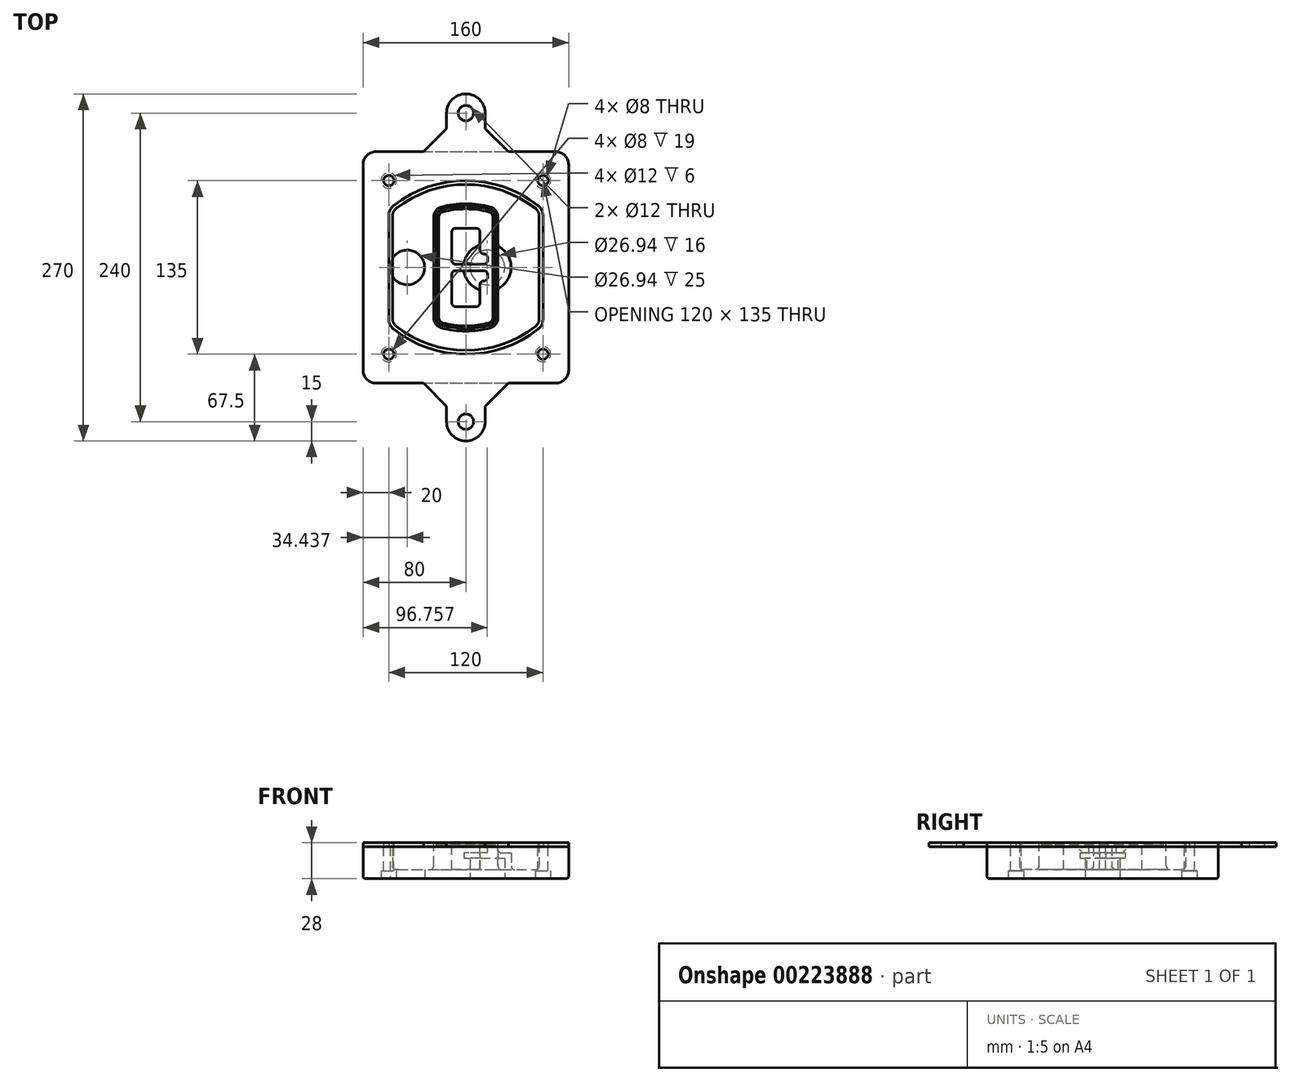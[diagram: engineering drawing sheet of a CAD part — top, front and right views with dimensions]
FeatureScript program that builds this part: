
annotation { "Feature Type Name" : "Feature", "Feature Type Description" : "" }
export const myFeature = defineFeature(function(context is Context, id is Id, definition is map)
    precondition{}
    {
        {
            var Q0;
            Q0=qCreatedBy(makeId("Top.planeOp"),FACE);
            var sketch = newSketch(context, id + "F0", { "sketchPlane" : qUnion([Q0])});
            skPoint(sketch, "E0.rect.middle", {"position": v(0, 0) * mm});
            skLineSegment(sketch, "E1.bottom", {"start": v(-70, -90) * mm, "end": v(70, -90) * mm});
            skLineSegment(sketch, "E1.top", {"start": v(-70, 90) * mm, "end": v(70, 90) * mm});
            skLineSegment(sketch, "E1.left", {"start": v(-80, -80) * mm, "end": v(-80, 80) * mm});
            skLineSegment(sketch, "E1.right", {"start": v(80, -80) * mm, "end": v(80, 80) * mm});
            skLineSegment(sketch, "E2", {"start": v(-80, 90) * mm, "end": v(80, -90) * mm, "construction": true});
            skLineSegment(sketch, "E3", {"start": v(80, 90) * mm, "end": v(-80, -90) * mm, "construction": true});
            skCircle(sketch, "E4", {"center": v(-60, 67.5) * mm, "radius": 4 * mm});
            skCircle(sketch, "E5", {"center": v(60, 67.5) * mm, "radius": 4 * mm});
            skCircle(sketch, "E6", {"center": v(60, -67.5) * mm, "radius": 4 * mm});
            skCircle(sketch, "E7", {"center": v(-60, -67.5) * mm, "radius": 4 * mm});
            skLineSegment(sketch, "E8", {"start": v(-60, 67.5) * mm, "end": v(60, 67.5) * mm, "construction": true});
            skLineSegment(sketch, "E9", {"start": v(60, 67.5) * mm, "end": v(60, -67.5) * mm, "construction": true});
            skLineSegment(sketch, "E10", {"start": v(60, -67.5) * mm, "end": v(-60, -67.5) * mm, "construction": true});
            skLineSegment(sketch, "E11", {"start": v(-60, -67.5) * mm, "end": v(-60, 67.5) * mm, "construction": true});
            skLineSegment(sketch, "E12", {"start": v(-60, 40.3) * mm, "end": v(-60, -40.3) * mm});
            skLineSegment(sketch, "E13", {"start": v(60, 40.3) * mm, "end": v(60, -40.3) * mm});
            skArc(sketch, "E14", {"start": v(56.15, 48.18) * mm, "mid": v(0, 67.5) * mm, "end": v(-56.15, 48.18) * mm});
            skArc(sketch, "E15", {"start": v(-56.15, -48.18) * mm, "mid": v(0, -67.5) * mm, "end": v(56.15, -48.18) * mm});
            skLineSegment(sketch, "E16", {"start": v(-60, 0) * mm, "end": v(60, 0) * mm, "construction": true});
            skPoint(sketch, "E17.visualSharp", {"position": v(-60, -45) * mm});
            skArc(sketch, "E17.filletArc", {"start": v(-60, -40.3) * mm, "mid": v(-58.99, -44.68) * mm, "end": v(-56.15, -48.18) * mm});
            skPoint(sketch, "E18.visualSharp", {"position": v(-60, 45) * mm});
            skArc(sketch, "E18.filletArc", {"start": v(-56.15, 48.18) * mm, "mid": v(-58.99, 44.68) * mm, "end": v(-60, 40.3) * mm});
            skPoint(sketch, "E19.visualSharp", {"position": v(60, 45) * mm});
            skArc(sketch, "E19.filletArc", {"start": v(60, 40.3) * mm, "mid": v(58.99, 44.68) * mm, "end": v(56.15, 48.18) * mm});
            skPoint(sketch, "E20.visualSharp", {"position": v(60, -45) * mm});
            skArc(sketch, "E20.filletArc", {"start": v(56.15, -48.18) * mm, "mid": v(58.99, -44.68) * mm, "end": v(60, -40.3) * mm});
            skPoint(sketch, "E21.visualSharp", {"position": v(-80, 90) * mm});
            skArc(sketch, "E21.filletArc", {"start": v(-70, 90) * mm, "mid": v(-77.07, 87.07) * mm, "end": v(-80, 80) * mm});
            skPoint(sketch, "E22.visualSharp", {"position": v(80, 90) * mm});
            skArc(sketch, "E22.filletArc", {"start": v(80, 80) * mm, "mid": v(77.07, 87.07) * mm, "end": v(70, 90) * mm});
            skPoint(sketch, "E23.visualSharp", {"position": v(80, -90) * mm});
            skArc(sketch, "E23.filletArc", {"start": v(70, -90) * mm, "mid": v(77.07, -87.07) * mm, "end": v(80, -80) * mm});
            skPoint(sketch, "E24.visualSharp", {"position": v(-80, -90) * mm});
            skArc(sketch, "E24.filletArc", {"start": v(-80, -80) * mm, "mid": v(-77.07, -87.07) * mm, "end": v(-70, -90) * mm});
            skArc(sketch, "E25.0", {"start": v(57, 40.3) * mm, "mid": v(56.3, 43.36) * mm, "end": v(54.3, 45.81) * mm});
            skLineSegment(sketch, "E25.1", {"start": v(57, 40.3) * mm, "end": v(57, -40.3) * mm});
            skArc(sketch, "E25.2", {"start": v(54.3, -45.81) * mm, "mid": v(56.3, -43.36) * mm, "end": v(57, -40.3) * mm});
            skArc(sketch, "E25.3", {"start": v(-54.3, -45.81) * mm, "mid": v(0, -64.5) * mm, "end": v(54.3, -45.81) * mm});
            skArc(sketch, "E25.4", {"start": v(-57, -40.3) * mm, "mid": v(-56.3, -43.36) * mm, "end": v(-54.3, -45.81) * mm});
            skArc(sketch, "E25.5", {"start": v(54.3, 45.81) * mm, "mid": v(0, 64.5) * mm, "end": v(-54.3, 45.81) * mm});
            skLineSegment(sketch, "E25.6", {"start": v(-57, 40.3) * mm, "end": v(-57, -40.3) * mm});
            skArc(sketch, "E25.7", {"start": v(-54.3, 45.81) * mm, "mid": v(-56.3, 43.36) * mm, "end": v(-57, 40.3) * mm});
            skArc(sketch, "E26.0", {"start": v(-58.62, 51.33) * mm, "mid": v(-62.58, 46.43) * mm, "end": v(-64, 40.3) * mm});
            skArc(sketch, "E26.1", {"start": v(58.62, 51.33) * mm, "mid": v(0, 71.5) * mm, "end": v(-58.62, 51.33) * mm});
            skArc(sketch, "E26.2", {"start": v(64, 40.3) * mm, "mid": v(62.58, 46.43) * mm, "end": v(58.62, 51.33) * mm});
            skLineSegment(sketch, "E26.3", {"start": v(64, 40.3) * mm, "end": v(64, -40.3) * mm});
            skArc(sketch, "E26.4", {"start": v(58.62, -51.33) * mm, "mid": v(62.58, -46.43) * mm, "end": v(64, -40.3) * mm});
            skLineSegment(sketch, "E26.5", {"start": v(-64, 40.3) * mm, "end": v(-64, -40.3) * mm});
            skArc(sketch, "E26.6", {"start": v(-58.62, -51.33) * mm, "mid": v(0, -71.5) * mm, "end": v(58.62, -51.33) * mm});
            skArc(sketch, "E26.7", {"start": v(-64, -40.3) * mm, "mid": v(-62.58, -46.43) * mm, "end": v(-58.62, -51.33) * mm});
            skSolve(sketch);
        }
        {
            var Q0;
            Q0=makeQuery(id+"F0.imprint","IMPRINT",FACE,{"disambiguationData":[TD([[makeQuery(id+"F0.imprint","IMPRINT",EDGE,{"derivedFrom":sQuery(id+"F0.wireOp",EDGE,"E1.bottom")}),1.0]])]});
            var Q1;
            Q1=makeQuery(id+"F0.imprint","IMPRINT",FACE,{"disambiguationData":[TD([[makeQuery(id+"F0.imprint","IMPRINT",EDGE,{"derivedFrom":sQuery(id+"F0.wireOp",EDGE,"E12")}),1.0]])]});
            var Q2;
            Q2=makeQuery(id+"F0.imprint","IMPRINT",FACE,{"disambiguationData":[TD([[makeQuery(id+"F0.imprint","IMPRINT",EDGE,{"derivedFrom":sQuery(id+"F0.wireOp",EDGE,"E25.0")}),1.0]])]});
            var Q3;
            Q3=makeQuery(id+"F0.imprint","IMPRINT",FACE,{"disambiguationData":[TD([[makeQuery(id+"F0.imprint","IMPRINT",EDGE,{"derivedFrom":sQuery(id+"F0.wireOp",EDGE,"E12")}),-1.0]])]});
            extrude(context, id + "F1", {"entities" : qUnion([Q0, Q1, Q2, Q3]), "oppositeDirection" : true, "depth" : 25 * mm});
        }
        {
            var Q0;
            Q0=makeQuery(id+"F0.imprint","IMPRINT",FACE,{"disambiguationData":[TD([[makeQuery(id+"F0.imprint","IMPRINT",EDGE,{"derivedFrom":sQuery(id+"F0.wireOp",EDGE,"E12")}),1.0]])]});
            extrude(context, id + "F2", {"entities" : qUnion([Q0]), "operationType" : NewBodyOperationType.ADD, "depth" : 3 * mm});
        }
        {
            var Q0;
            Q0=makeQuery(id+"F0.imprint","IMPRINT",FACE,{"disambiguationData":[TD([[makeQuery(id+"F0.imprint","IMPRINT",EDGE,{"derivedFrom":sQuery(id+"F0.wireOp",EDGE,"E25.0")}),1.0]])]});
            extrude(context, id + "F3", {"entities" : qUnion([Q0]), "operationType" : NewBodyOperationType.REMOVE, "oppositeDirection" : true, "depth" : 18 * mm});
        }
        {
            var Q0;
            Q0=makeQuery(id+"F2.opExtrude","CAP_FACE",FACE,{"disambiguationData":[OSD([sQuery(id+"F0.wireOp",EDGE,"E12"),sQuery(id+"F0.wireOp",EDGE,"E13"),sQuery(id+"F0.wireOp",EDGE,"E14"),sQuery(id+"F0.wireOp",EDGE,"E15"),sQuery(id+"F0.wireOp",EDGE,"E17.filletArc"),sQuery(id+"F0.wireOp",EDGE,"E18.filletArc"),sQuery(id+"F0.wireOp",EDGE,"E19.filletArc"),sQuery(id+"F0.wireOp",EDGE,"E20.filletArc"),sQuery(id+"F0.wireOp",EDGE,"E25.0"),sQuery(id+"F0.wireOp",EDGE,"E25.1"),sQuery(id+"F0.wireOp",EDGE,"E25.2"),sQuery(id+"F0.wireOp",EDGE,"E25.3"),sQuery(id+"F0.wireOp",EDGE,"E25.4"),sQuery(id+"F0.wireOp",EDGE,"E25.5"),sQuery(id+"F0.wireOp",EDGE,"E25.6"),sQuery(id+"F0.wireOp",EDGE,"E25.7")])],"isStart":false});
            var sketch = newSketch(context, id + "F4", { "sketchPlane" : qUnion([Q0])});
            skArc(sketch, "E27.0", {"start": v(-19.08, -46.97) * mm, "mid": v(0, -49.5) * mm, "end": v(19.08, -46.97) * mm});
            skArc(sketch, "E28.0", {"start": v(19.08, 46.97) * mm, "mid": v(0, 49.5) * mm, "end": v(-19.08, 46.97) * mm});
            skLineSegment(sketch, "E29", {"start": v(-25, 39.25) * mm, "end": v(-25, -39.25) * mm});
            skLineSegment(sketch, "E30", {"start": v(25, 39.25) * mm, "end": v(25, -39.25) * mm});
            skLineSegment(sketch, "E31", {"start": v(-25, 45.1) * mm, "end": v(25, 45.1) * mm, "construction": true});
            skLineSegment(sketch, "E32", {"start": v(-25, -45.1) * mm, "end": v(25, -45.1) * mm, "construction": true});
            skPoint(sketch, "E33.visualSharp", {"position": v(-25, 45.1) * mm});
            skArc(sketch, "E33.filletArc", {"start": v(-19.08, 46.97) * mm, "mid": v(-23.35, 44.11) * mm, "end": v(-25, 39.25) * mm});
            skPoint(sketch, "E34.visualSharp", {"position": v(25, 45.1) * mm});
            skArc(sketch, "E34.filletArc", {"start": v(25, 39.25) * mm, "mid": v(23.35, 44.11) * mm, "end": v(19.08, 46.97) * mm});
            skPoint(sketch, "E35.visualSharp", {"position": v(25, -45.1) * mm});
            skArc(sketch, "E35.filletArc", {"start": v(19.08, -46.97) * mm, "mid": v(23.35, -44.11) * mm, "end": v(25, -39.25) * mm});
            skPoint(sketch, "E36.visualSharp", {"position": v(-25, -45.1) * mm});
            skArc(sketch, "E36.filletArc", {"start": v(-25, -39.25) * mm, "mid": v(-23.35, -44.11) * mm, "end": v(-19.08, -46.97) * mm});
            skArc(sketch, "E37.0", {"start": v(54.3, 45.81) * mm, "mid": v(0, 64.5) * mm, "end": v(-54.3, 45.81) * mm});
            skArc(sketch, "E37.1", {"start": v(-54.3, 45.81) * mm, "mid": v(-56.3, 43.36) * mm, "end": v(-57, 40.3) * mm});
            skLineSegment(sketch, "E37.2", {"start": v(-57, 40.3) * mm, "end": v(-57, -40.3) * mm});
            skArc(sketch, "E37.3", {"start": v(-57, -40.3) * mm, "mid": v(-56.3, -43.36) * mm, "end": v(-54.3, -45.81) * mm});
            skArc(sketch, "E37.4", {"start": v(-54.3, -45.81) * mm, "mid": v(0, -64.5) * mm, "end": v(54.3, -45.81) * mm});
            skArc(sketch, "E37.5", {"start": v(54.3, -45.81) * mm, "mid": v(56.3, -43.36) * mm, "end": v(57, -40.3) * mm});
            skLineSegment(sketch, "E37.6", {"start": v(57, 40.3) * mm, "end": v(57, -40.3) * mm});
            skArc(sketch, "E37.7", {"start": v(57, 40.3) * mm, "mid": v(56.3, 43.36) * mm, "end": v(54.3, 45.81) * mm});
            skLineSegment(sketch, "E38.0", {"start": v(23, 39.25) * mm, "end": v(23, -39.25) * mm});
            skArc(sketch, "E38.1", {"start": v(18.56, -45.04) * mm, "mid": v(21.76, -42.9) * mm, "end": v(23, -39.25) * mm});
            skArc(sketch, "E38.2", {"start": v(-18.56, -45.04) * mm, "mid": v(0, -47.5) * mm, "end": v(18.56, -45.04) * mm});
            skArc(sketch, "E38.3", {"start": v(-23, -39.25) * mm, "mid": v(-21.76, -42.9) * mm, "end": v(-18.56, -45.04) * mm});
            skLineSegment(sketch, "E38.4", {"start": v(-23, 39.25) * mm, "end": v(-23, -39.25) * mm});
            skArc(sketch, "E38.5", {"start": v(23, 39.25) * mm, "mid": v(21.76, 42.9) * mm, "end": v(18.56, 45.04) * mm});
            skArc(sketch, "E38.6", {"start": v(-18.56, 45.04) * mm, "mid": v(-21.76, 42.9) * mm, "end": v(-23, 39.25) * mm});
            skArc(sketch, "E38.7", {"start": v(18.56, 45.04) * mm, "mid": v(0, 47.5) * mm, "end": v(-18.56, 45.04) * mm});
            skArc(sketch, "E39.0", {"start": v(21, 39.25) * mm, "mid": v(20.18, 41.68) * mm, "end": v(18.04, 43.1) * mm});
            skLineSegment(sketch, "E39.1", {"start": v(21, 39.25) * mm, "end": v(21, -39.25) * mm});
            skArc(sketch, "E39.2", {"start": v(18.04, -43.1) * mm, "mid": v(20.18, -41.68) * mm, "end": v(21, -39.25) * mm});
            skArc(sketch, "E39.3", {"start": v(-18.04, -43.1) * mm, "mid": v(0, -45.5) * mm, "end": v(18.04, -43.1) * mm});
            skArc(sketch, "E39.4", {"start": v(-21, -39.25) * mm, "mid": v(-20.18, -41.68) * mm, "end": v(-18.04, -43.1) * mm});
            skArc(sketch, "E39.5", {"start": v(18.04, 43.1) * mm, "mid": v(0, 45.5) * mm, "end": v(-18.04, 43.1) * mm});
            skLineSegment(sketch, "E39.6", {"start": v(-21, 39.25) * mm, "end": v(-21, -39.25) * mm});
            skArc(sketch, "E39.7", {"start": v(-18.04, 43.1) * mm, "mid": v(-20.18, 41.68) * mm, "end": v(-21, 39.25) * mm});
            skLineSegment(sketch, "E40", {"start": v(-25, 0) * mm, "end": v(25, 0) * mm, "construction": true});
            skLineSegment(sketch, "E41", {"start": v(-11, 5.5) * mm, "end": v(-11, 27.5) * mm});
            skLineSegment(sketch, "E42", {"start": v(-8, 30.5) * mm, "end": v(8, 30.5) * mm});
            skLineSegment(sketch, "E43", {"start": v(11, 27.5) * mm, "end": v(11, 13.5) * mm});
            skLineSegment(sketch, "E44", {"start": v(14, 10.5) * mm, "end": v(14, 10.5) * mm});
            skLineSegment(sketch, "E45", {"start": v(17, 7.5) * mm, "end": v(17, 5.5) * mm});
            skLineSegment(sketch, "E46", {"start": v(14, 2.5) * mm, "end": v(-8, 2.5) * mm});
            skPoint(sketch, "E47.visualSharp", {"position": v(-11, 30.5) * mm});
            skArc(sketch, "E47.filletArc", {"start": v(-8, 30.5) * mm, "mid": v(-10.12, 29.62) * mm, "end": v(-11, 27.5) * mm});
            skPoint(sketch, "E48.visualSharp", {"position": v(11, 30.5) * mm});
            skArc(sketch, "E48.filletArc", {"start": v(11, 27.5) * mm, "mid": v(10.12, 29.62) * mm, "end": v(8, 30.5) * mm});
            skPoint(sketch, "E49.visualSharp", {"position": v(11, 10.5) * mm});
            skArc(sketch, "E49.filletArc", {"start": v(11, 13.5) * mm, "mid": v(11.88, 11.38) * mm, "end": v(14, 10.5) * mm});
            skPoint(sketch, "E50.visualSharp", {"position": v(17, 10.5) * mm});
            skArc(sketch, "E50.filletArc", {"start": v(17, 7.5) * mm, "mid": v(16.12, 9.62) * mm, "end": v(14, 10.5) * mm});
            skPoint(sketch, "E51.visualSharp", {"position": v(17, 2.5) * mm});
            skArc(sketch, "E51.filletArc", {"start": v(14, 2.5) * mm, "mid": v(16.12, 3.38) * mm, "end": v(17, 5.5) * mm});
            skPoint(sketch, "E52.visualSharp", {"position": v(-11, 2.5) * mm});
            skArc(sketch, "E52.filletArc", {"start": v(-11, 5.5) * mm, "mid": v(-10.12, 3.38) * mm, "end": v(-8, 2.5) * mm});
            skLineSegment(sketch, "E53.0.MirrorCS", {"start": v(14, -2.5) * mm, "end": v(-8, -2.5) * mm});
            skArc(sketch, "E54.0.MirrorCS", {"start": v(-11, -5.5) * mm, "mid": v(-10.12, -3.38) * mm, "end": v(-8, -2.5) * mm});
            skLineSegment(sketch, "E55.0.MirrorCS", {"start": v(-11, -5.5) * mm, "end": v(-11, -27.5) * mm});
            skArc(sketch, "E56.0.MirrorCS", {"start": v(-8, -30.5) * mm, "mid": v(-10.12, -29.62) * mm, "end": v(-11, -27.5) * mm});
            skLineSegment(sketch, "E57.0.MirrorCS", {"start": v(-8, -30.5) * mm, "end": v(8, -30.5) * mm});
            skArc(sketch, "E58.0.MirrorCS", {"start": v(11, -27.5) * mm, "mid": v(10.12, -29.62) * mm, "end": v(8, -30.5) * mm});
            skLineSegment(sketch, "E59.0.MirrorCS", {"start": v(11, -27.5) * mm, "end": v(11, -13.5) * mm});
            skArc(sketch, "E60.0.MirrorCS", {"start": v(11, -13.5) * mm, "mid": v(11.88, -11.38) * mm, "end": v(14, -10.5) * mm});
            skArc(sketch, "E61.0.MirrorCS", {"start": v(17, -7.5) * mm, "mid": v(16.12, -9.62) * mm, "end": v(14, -10.5) * mm});
            skLineSegment(sketch, "E62.0.MirrorCS", {"start": v(17, -7.5) * mm, "end": v(17, -5.5) * mm});
            skArc(sketch, "E63.0.MirrorCS", {"start": v(14, -2.5) * mm, "mid": v(16.12, -3.38) * mm, "end": v(17, -5.5) * mm});
            skSolve(sketch);
        }
        {
            var Q0;
            Q0=makeQuery(id+"F4.imprint","IMPRINT",FACE,{"disambiguationData":[TD([[makeQuery(id+"F4.imprint","IMPRINT",EDGE,{"derivedFrom":sQuery(id+"F4.wireOp",EDGE,"E27.0")}),1.0]])]});
            var Q1;
            Q1=makeQuery(id+"F4.imprint","IMPRINT",FACE,{"disambiguationData":[TD([[makeQuery(id+"F4.imprint","IMPRINT",EDGE,{"derivedFrom":sQuery(id+"F4.wireOp",EDGE,"E38.0")}),-1.0]])]});
            var Q2;
            Q2=makeQuery(id+"F4.imprint","IMPRINT",FACE,{"disambiguationData":[TD([[makeQuery(id+"F4.imprint","IMPRINT",EDGE,{"derivedFrom":sQuery(id+"F4.wireOp",EDGE,"E39.0")}),1.0]])]});
            extrude(context, id + "F5", {"entities" : qUnion([Q0, Q1, Q2]), "operationType" : NewBodyOperationType.ADD, "endBound" : BoundingType.UP_TO_NEXT, "oppositeDirection" : true, "depth" : 25 * mm});
        }
        {
            var Q0;
            Q0=makeQuery(id+"F4.imprint","IMPRINT",FACE,{"disambiguationData":[TD([[makeQuery(id+"F4.imprint","IMPRINT",EDGE,{"derivedFrom":sQuery(id+"F4.wireOp",EDGE,"E38.0")}),-1.0]])]});
            extrude(context, id + "F6", {"entities" : qUnion([Q0]), "operationType" : NewBodyOperationType.REMOVE, "oppositeDirection" : true, "depth" : 2 * mm});
        }
        {
            var Q0;
            Q0=makeQuery(id+"F1.opExtrude","CAP_FACE",FACE,{"disambiguationData":[OSD([sQuery(id+"F0.wireOp",EDGE,"E1.bottom"),sQuery(id+"F0.wireOp",EDGE,"E1.top"),sQuery(id+"F0.wireOp",EDGE,"E1.left"),sQuery(id+"F0.wireOp",EDGE,"E1.right"),sQuery(id+"F0.wireOp",EDGE,"E4"),sQuery(id+"F0.wireOp",EDGE,"E5"),sQuery(id+"F0.wireOp",EDGE,"E6"),sQuery(id+"F0.wireOp",EDGE,"E7"),sQuery(id+"F0.wireOp",EDGE,"E21.filletArc"),sQuery(id+"F0.wireOp",EDGE,"E22.filletArc"),sQuery(id+"F0.wireOp",EDGE,"E23.filletArc"),sQuery(id+"F0.wireOp",EDGE,"E24.filletArc")])],"isStart":false});
            var sketch = newSketch(context, id + "F7", { "sketchPlane" : qUnion([Q0])});
            skCircle(sketch, "E64", {"center": v(16.76, 0) * mm, "radius": 13.47 * mm});
            skCircle(sketch, "E65", {"center": v(-45.56, 0) * mm, "radius": 13.47 * mm});
            skLineSegment(sketch, "E66", {"start": v(80, 0) * mm, "end": v(-80, 0) * mm});
            skCircle(sketch, "E67", {"center": v(16.76, 0) * mm, "radius": 18.47 * mm});
            skCircle(sketch, "E68", {"center": v(60, -67.5) * mm, "radius": 6 * mm});
            skCircle(sketch, "E69", {"center": v(-60, -67.5) * mm, "radius": 6 * mm});
            skCircle(sketch, "E70", {"center": v(-60, 67.5) * mm, "radius": 6 * mm});
            skCircle(sketch, "E71", {"center": v(60, 67.5) * mm, "radius": 6 * mm});
            skSolve(sketch);
        }
        {
            var Q0;
            {var subQ1=sQuery(id+"F7.wireOp",EDGE,"E66");var subQ4=sQuery(id+"F7.wireOp",EDGE,"E64");var subQ6=makeQuery(id+"F7.imprint","INTERSECT",VERTEX,{"disambiguationData":[OD(0.0)],"derivedFrom":[subQ4,subQ1]});Q0=makeQuery(id+"F7.imprint","IMPRINT",FACE,{"disambiguationData":[TD([[makeQuery(id+"F7.imprint","IMPRINT",EDGE,{"disambiguationData":[TD([[subQ6,-1.0]])],"derivedFrom":subQ4}),-1.0]])]});}
            var Q1;
            {var subQ0=sQuery(id+"F7.wireOp",EDGE,"E66");var subQ1=sQuery(id+"F7.wireOp",EDGE,"E64");var subQ3=makeQuery(id+"F7.imprint","INTERSECT",VERTEX,{"disambiguationData":[OD(0.0)],"derivedFrom":[subQ1,subQ0]});Q1=makeQuery(id+"F7.imprint","IMPRINT",FACE,{"disambiguationData":[TD([[makeQuery(id+"F7.imprint","IMPRINT",EDGE,{"disambiguationData":[TD([[subQ3,-1.0]])],"derivedFrom":subQ1}),1.0]])]});}
            var Q2;
            {var subQ0=sQuery(id+"F7.wireOp",EDGE,"E66");var subQ1=sQuery(id+"F7.wireOp",EDGE,"E64");var subQ3=makeQuery(id+"F7.imprint","INTERSECT",VERTEX,{"disambiguationData":[OD(0.0)],"derivedFrom":[subQ1,subQ0]});Q2=makeQuery(id+"F7.imprint","IMPRINT",FACE,{"disambiguationData":[TD([[makeQuery(id+"F7.imprint","IMPRINT",EDGE,{"disambiguationData":[TD([[subQ3,1.0]])],"derivedFrom":subQ1}),1.0]])]});}
            var Q3;
            {var subQ1=sQuery(id+"F7.wireOp",EDGE,"E66");var subQ4=sQuery(id+"F7.wireOp",EDGE,"E64");var subQ6=makeQuery(id+"F7.imprint","INTERSECT",VERTEX,{"disambiguationData":[OD(0.0)],"derivedFrom":[subQ4,subQ1]});Q3=makeQuery(id+"F7.imprint","IMPRINT",FACE,{"disambiguationData":[TD([[makeQuery(id+"F7.imprint","IMPRINT",EDGE,{"disambiguationData":[TD([[subQ6,1.0]])],"derivedFrom":subQ4}),-1.0]])]});}
            extrude(context, id + "F8", {"entities" : qUnion([Q0, Q1, Q2, Q3]), "operationType" : NewBodyOperationType.ADD, "oppositeDirection" : true, "depth" : 20 * mm});
        }
        {
            var Q0;
            {var subQ0=sQuery(id+"F7.wireOp",EDGE,"E66");var subQ1=sQuery(id+"F7.wireOp",EDGE,"E64");var subQ3=makeQuery(id+"F7.imprint","INTERSECT",VERTEX,{"disambiguationData":[OD(0.0)],"derivedFrom":[subQ1,subQ0]});Q0=makeQuery(id+"F7.imprint","IMPRINT",FACE,{"disambiguationData":[TD([[makeQuery(id+"F7.imprint","IMPRINT",EDGE,{"disambiguationData":[TD([[subQ3,-1.0]])],"derivedFrom":subQ1}),1.0]])]});}
            var Q1;
            {var subQ0=sQuery(id+"F7.wireOp",EDGE,"E66");var subQ1=sQuery(id+"F7.wireOp",EDGE,"E64");var subQ3=makeQuery(id+"F7.imprint","INTERSECT",VERTEX,{"disambiguationData":[OD(0.0)],"derivedFrom":[subQ1,subQ0]});Q1=makeQuery(id+"F7.imprint","IMPRINT",FACE,{"disambiguationData":[TD([[makeQuery(id+"F7.imprint","IMPRINT",EDGE,{"disambiguationData":[TD([[subQ3,1.0]])],"derivedFrom":subQ1}),1.0]])]});}
            extrude(context, id + "F9", {"entities" : qUnion([Q0, Q1]), "operationType" : NewBodyOperationType.REMOVE, "oppositeDirection" : true, "depth" : 16 * mm});
        }
        {
            var Q0;
            {var subQ0=sQuery(id+"F7.wireOp",EDGE,"E66");var subQ1=sQuery(id+"F7.wireOp",EDGE,"E65");var subQ3=makeQuery(id+"F7.imprint","INTERSECT",VERTEX,{"disambiguationData":[OD(0.0)],"derivedFrom":[subQ1,subQ0]});Q0=makeQuery(id+"F7.imprint","IMPRINT",FACE,{"disambiguationData":[TD([[makeQuery(id+"F7.imprint","IMPRINT",EDGE,{"disambiguationData":[TD([[subQ3,-1.0]])],"derivedFrom":subQ1}),1.0]])]});}
            var Q1;
            {var subQ0=sQuery(id+"F7.wireOp",EDGE,"E66");var subQ1=sQuery(id+"F7.wireOp",EDGE,"E65");var subQ3=makeQuery(id+"F7.imprint","INTERSECT",VERTEX,{"disambiguationData":[OD(0.0)],"derivedFrom":[subQ1,subQ0]});Q1=makeQuery(id+"F7.imprint","IMPRINT",FACE,{"disambiguationData":[TD([[makeQuery(id+"F7.imprint","IMPRINT",EDGE,{"disambiguationData":[TD([[subQ3,1.0]])],"derivedFrom":subQ1}),1.0]])]});}
            extrude(context, id + "F10", {"entities" : qUnion([Q0, Q1]), "operationType" : NewBodyOperationType.REMOVE, "oppositeDirection" : true, "depth" : 25 * mm});
        }
        {
            var Q0;
            Q0=makeQuery(id+"F7.imprint","IMPRINT",FACE,{"disambiguationData":[TD([[makeQuery(id+"F7.imprint","IMPRINT",EDGE,{"derivedFrom":sQuery(id+"F7.wireOp",EDGE,"E68")}),1.0]])]});
            var Q1;
            Q1=makeQuery(id+"F7.imprint","IMPRINT",FACE,{"disambiguationData":[TD([[makeQuery(id+"F7.imprint","IMPRINT",EDGE,{"derivedFrom":makeQuery(id+"F1.opExtrude","CAP_EDGE",EDGE,{"disambiguationData":[OSD([sQuery(id+"F0.wireOp",EDGE,"E5")])],"isStart":false})}),-1.0]])]});
            var Q2;
            Q2=makeQuery(id+"F7.imprint","IMPRINT",FACE,{"disambiguationData":[TD([[makeQuery(id+"F7.imprint","IMPRINT",EDGE,{"derivedFrom":sQuery(id+"F7.wireOp",EDGE,"E69")}),1.0]])]});
            var Q3;
            Q3=makeQuery(id+"F7.imprint","IMPRINT",FACE,{"disambiguationData":[TD([[makeQuery(id+"F7.imprint","IMPRINT",EDGE,{"derivedFrom":makeQuery(id+"F1.opExtrude","CAP_EDGE",EDGE,{"disambiguationData":[OSD([sQuery(id+"F0.wireOp",EDGE,"E4")])],"isStart":false})}),-1.0]])]});
            var Q4;
            Q4=makeQuery(id+"F7.imprint","IMPRINT",FACE,{"disambiguationData":[TD([[makeQuery(id+"F7.imprint","IMPRINT",EDGE,{"derivedFrom":sQuery(id+"F7.wireOp",EDGE,"E70")}),1.0]])]});
            var Q5;
            Q5=makeQuery(id+"F7.imprint","IMPRINT",FACE,{"disambiguationData":[TD([[makeQuery(id+"F7.imprint","IMPRINT",EDGE,{"derivedFrom":makeQuery(id+"F1.opExtrude","CAP_EDGE",EDGE,{"disambiguationData":[OSD([sQuery(id+"F0.wireOp",EDGE,"E7")])],"isStart":false})}),-1.0]])]});
            var Q6;
            Q6=makeQuery(id+"F7.imprint","IMPRINT",FACE,{"disambiguationData":[TD([[makeQuery(id+"F7.imprint","IMPRINT",EDGE,{"derivedFrom":sQuery(id+"F7.wireOp",EDGE,"E71")}),1.0]])]});
            var Q7;
            Q7=makeQuery(id+"F7.imprint","IMPRINT",FACE,{"disambiguationData":[TD([[makeQuery(id+"F7.imprint","IMPRINT",EDGE,{"derivedFrom":makeQuery(id+"F1.opExtrude","CAP_EDGE",EDGE,{"disambiguationData":[OSD([sQuery(id+"F0.wireOp",EDGE,"E6")])],"isStart":false})}),-1.0]])]});
            extrude(context, id + "F11", {"entities" : qUnion([Q0, Q1, Q2, Q3, Q4, Q5, Q6, Q7]), "operationType" : NewBodyOperationType.REMOVE, "oppositeDirection" : true, "depth" : 6 * mm});
        }
        {
            var Q0;
            Q0=makeQuery(id+"F9.boolean.opBoolean","COPY",FACE,{"derivedFrom":makeQuery(id+"F9.opExtrude","CAP_FACE",FACE,{"disambiguationData":[OSD([sQuery(id+"F7.wireOp",EDGE,"E64")])],"isStart":false})});
            var sketch = newSketch(context, id + "F12", { "sketchPlane" : qUnion([Q0])});
            skArc(sketch, "E72.0", {"start": v(11, 17.55) * mm, "mid": v(2.57, 11.82) * mm, "end": v(-1.54, 2.5) * mm});
            skArc(sketch, "E72.1", {"start": v(-1.54, -2.5) * mm, "mid": v(2.57, -11.82) * mm, "end": v(11, -17.55) * mm});
            skLineSegment(sketch, "E73", {"start": v(-1.54, -2.5) * mm, "end": v(14, -2.5) * mm});
            skLineSegment(sketch, "E74.0", {"start": v(14, 2.5) * mm, "end": v(-1.54, 2.5) * mm});
            skArc(sketch, "E74.1", {"start": v(14, 2.5) * mm, "mid": v(16.12, 3.38) * mm, "end": v(17, 5.5) * mm});
            skLineSegment(sketch, "E74.2", {"start": v(17, 7.5) * mm, "end": v(17, 5.5) * mm});
            skArc(sketch, "E74.3", {"start": v(17, 7.5) * mm, "mid": v(16.12, 9.62) * mm, "end": v(14, 10.5) * mm});
            skArc(sketch, "E74.4", {"start": v(11, 13.5) * mm, "mid": v(11.88, 11.38) * mm, "end": v(14, 10.5) * mm});
            skLineSegment(sketch, "E74.5", {"start": v(11, 17.55) * mm, "end": v(11, 13.5) * mm});
            skLineSegment(sketch, "E74.7", {"start": v(14, -2.5) * mm, "end": v(-1.54, -2.5) * mm});
            skArc(sketch, "E74.8", {"start": v(14, -2.5) * mm, "mid": v(16.12, -3.38) * mm, "end": v(17, -5.5) * mm});
            skLineSegment(sketch, "E74.9", {"start": v(17, -7.5) * mm, "end": v(17, -5.5) * mm});
            skArc(sketch, "E74.10", {"start": v(17, -7.5) * mm, "mid": v(16.12, -9.62) * mm, "end": v(14, -10.5) * mm});
            skArc(sketch, "E74.11", {"start": v(11, -13.5) * mm, "mid": v(11.88, -11.38) * mm, "end": v(14, -10.5) * mm});
            skLineSegment(sketch, "E74.12", {"start": v(11, -17.55) * mm, "end": v(11, -13.5) * mm});
            skPoint(sketch, "E75.orphan", {"position": v(11, -27.5) * mm});
            skPoint(sketch, "E76.orphan", {"position": v(-8, -2.5) * mm});
            skPoint(sketch, "E77.orphan", {"position": v(-8, 2.5) * mm});
            skPoint(sketch, "E78.orphan", {"position": v(11, 27.5) * mm});
            skSolve(sketch);
        }
        {
            var Q0;
            {var subQ7=sQuery(id+"F12.wireOp",EDGE,"E72.0");var subQ14=sQuery(id+"F12.wireOp",EDGE,"E72.1");var subQ16=sQuery(id+"F12.wireOp",EDGE,"E74.1");var subQ18=sQuery(id+"F12.wireOp",EDGE,"E74.8");Q0=qUnion([makeQuery(id+"F12.imprint","IMPRINT",FACE,{"disambiguationData":[TD([[makeQuery(id+"F12.imprint","IMPRINT",EDGE,{"derivedFrom":subQ7}),1.0]])]}),makeQuery(id+"F12.imprint","IMPRINT",FACE,{"disambiguationData":[TD([[makeQuery(id+"F12.imprint","IMPRINT",EDGE,{"derivedFrom":subQ14}),1.0]])]}),makeQuery(id+"F12.imprint","IMPRINT",FACE,{"disambiguationData":[TD([[makeQuery(id+"F12.imprint","IMPRINT",EDGE,{"derivedFrom":subQ16}),1.0]])]}),makeQuery(id+"F12.imprint","IMPRINT",FACE,{"disambiguationData":[TD([[makeQuery(id+"F12.imprint","IMPRINT",EDGE,{"derivedFrom":subQ18}),-1.0]])]})]);}
            var Q1;
            Q1=makeQuery(id+"F5.boolean.opBoolean","SPLIT",FACE,{"disambiguationData":[TD([makeQuery(id+"F5.opExtrude","SWEPT_FACE",FACE,{"disambiguationData":[OSD([sQuery(id+"F4.wireOp",EDGE,"E41")])]})])],"derivedFrom":makeQuery(id+"F3.boolean.opBoolean","COPY",FACE,{"derivedFrom":makeQuery(id+"F3.opExtrude","CAP_FACE",FACE,{"disambiguationData":[OSD([sQuery(id+"F0.wireOp",EDGE,"E25.0"),sQuery(id+"F0.wireOp",EDGE,"E25.1"),sQuery(id+"F0.wireOp",EDGE,"E25.2"),sQuery(id+"F0.wireOp",EDGE,"E25.3"),sQuery(id+"F0.wireOp",EDGE,"E25.4"),sQuery(id+"F0.wireOp",EDGE,"E25.5"),sQuery(id+"F0.wireOp",EDGE,"E25.6"),sQuery(id+"F0.wireOp",EDGE,"E25.7")])],"isStart":false})})});
            extrude(context, id + "F13", {"entities" : qUnion([Q0]), "operationType" : NewBodyOperationType.REMOVE, "endBound" : BoundingType.UP_TO_SURFACE, "endBoundEntityFace" : qUnion([Q1]), "depth" : 25 * mm});
        }
        {
            var Q0;
            Q0=makeQuery(id+"F3.boolean.opBoolean","COPY",EDGE,{"derivedFrom":makeQuery(id+"F3.opExtrude","CAP_EDGE",EDGE,{"disambiguationData":[OSD([sQuery(id+"F0.wireOp",EDGE,"E25.6")])],"isStart":false})});
            var Q1;
            Q1=makeQuery(id+"F8.boolean.opBoolean","INTERSECT",EDGE,{"derivedFrom":[makeQuery(id+"F5.opExtrude","SWEPT_FACE",FACE,{"disambiguationData":[OSD([sQuery(id+"F4.wireOp",EDGE,"E30")])]}),makeQuery(id+"F8.opExtrude","CAP_FACE",FACE,{"disambiguationData":[OSD([sQuery(id+"F7.wireOp",EDGE,"E67")])],"isStart":false})]});
            var Q2;
            Q2=makeQuery(id+"F8.boolean.opBoolean","INTERSECT",EDGE,{"disambiguationData":[OD(1.0)],"derivedFrom":[makeQuery(id+"F5.opExtrude","SWEPT_FACE",FACE,{"disambiguationData":[OSD([sQuery(id+"F4.wireOp",EDGE,"E30")])]}),makeQuery(id+"F8.opExtrude","SWEPT_FACE",FACE,{"disambiguationData":[OSD([sQuery(id+"F7.wireOp",EDGE,"E67")])]})]});
            var Q3;
            {var subQ0=sQuery(id+"F4.wireOp",EDGE,"E30");Q3=makeQuery(id+"F8.boolean.opBoolean","SPLIT",EDGE,{"disambiguationData":[TD([makeQuery(id+"F5.opExtrude","SWEPT_FACE",FACE,{"disambiguationData":[OSD([sQuery(id+"F4.wireOp",EDGE,"E35.filletArc")])]})])],"derivedFrom":makeQuery(id+"F5.opExtrude","CAP_EDGE",EDGE,{"disambiguationData":[OSD([subQ0])],"isStart":false})});}
            var Q4;
            {var subQ0=sQuery(id+"F0.wireOp",EDGE,"E25.7");var subQ1=sQuery(id+"F0.wireOp",EDGE,"E25.1");var subQ2=sQuery(id+"F0.wireOp",EDGE,"E25.6");var subQ3=sQuery(id+"F0.wireOp",EDGE,"E25.5");var subQ4=sQuery(id+"F0.wireOp",EDGE,"E25.4");var subQ5=sQuery(id+"F0.wireOp",EDGE,"E25.0");var subQ6=sQuery(id+"F0.wireOp",EDGE,"E25.2");var subQ7=sQuery(id+"F0.wireOp",EDGE,"E25.3");Q4=makeQuery(id+"F8.boolean.opBoolean","INTERSECT",EDGE,{"derivedFrom":[makeQuery(id+"F5.boolean.opBoolean","SPLIT",FACE,{"disambiguationData":[TD([makeQuery(id+"F2.opExtrude","SWEPT_FACE",FACE,{"disambiguationData":[OSD([subQ5])]})])],"derivedFrom":makeQuery(id+"F3.boolean.opBoolean","COPY",FACE,{"derivedFrom":makeQuery(id+"F3.opExtrude","CAP_FACE",FACE,{"disambiguationData":[OSD([subQ5,subQ1,subQ6,subQ7,subQ4,subQ3,subQ2,subQ0])],"isStart":false})})}),makeQuery(id+"F8.opExtrude","SWEPT_FACE",FACE,{"disambiguationData":[OSD([sQuery(id+"F7.wireOp",EDGE,"E67")])]})]});}
            var Q5;
            Q5=makeQuery(id+"F8.boolean.opBoolean","INTERSECT",EDGE,{"disambiguationData":[OD(0.0)],"derivedFrom":[makeQuery(id+"F5.opExtrude","SWEPT_FACE",FACE,{"disambiguationData":[OSD([sQuery(id+"F4.wireOp",EDGE,"E30")])]}),makeQuery(id+"F8.opExtrude","SWEPT_FACE",FACE,{"disambiguationData":[OSD([sQuery(id+"F7.wireOp",EDGE,"E67")])]})]});
            fillet(context, id + "F14", {"entities" : qUnion([Q0, Q1, Q2, Q3, Q4, Q5]), "radius" : 3 * mm, "tangentPropagation" : true, "allowEdgeOverflow" : false});
        }
        {
            var Q0;
            Q0=makeQuery(id+"F1.opExtrude","CAP_EDGE",EDGE,{"disambiguationData":[OSD([sQuery(id+"F0.wireOp",EDGE,"E1.bottom")])],"isStart":false});
            fillet(context, id + "F15", {"entities" : qUnion([Q0]), "radius" : 2 * mm, "tangentPropagation" : true, "allowEdgeOverflow" : false});
        }
        {
            var Q0;
            {var subQ0=sQuery(id+"F0.wireOp",EDGE,"E22.filletArc");var subQ1=sQuery(id+"F0.wireOp",EDGE,"E7");var subQ2=sQuery(id+"F0.wireOp",EDGE,"E6");var subQ3=sQuery(id+"F0.wireOp",EDGE,"E5");var subQ4=sQuery(id+"F0.wireOp",EDGE,"E4");var subQ5=sQuery(id+"F0.wireOp",EDGE,"E1.bottom");var subQ6=sQuery(id+"F0.wireOp",EDGE,"E21.filletArc");var subQ7=sQuery(id+"F0.wireOp",EDGE,"E1.top");var subQ8=sQuery(id+"F0.wireOp",EDGE,"E1.left");var subQ9=sQuery(id+"F0.wireOp",EDGE,"E1.right");var subQ10=sQuery(id+"F0.wireOp",EDGE,"E23.filletArc");var subQ11=sQuery(id+"F0.wireOp",EDGE,"E24.filletArc");Q0=makeQuery(id+"F2.boolean.opBoolean","SPLIT",FACE,{"disambiguationData":[TD([makeQuery(id+"F1.opExtrude","SWEPT_FACE",FACE,{"disambiguationData":[OSD([subQ5])]})])],"derivedFrom":makeQuery(id+"F1.opExtrude","CAP_FACE",FACE,{"disambiguationData":[OSD([subQ5,subQ7,subQ8,subQ9,subQ4,subQ3,subQ2,subQ1,subQ6,subQ0,subQ10,subQ11])],"isStart":true})});}
            var sketch = newSketch(context, id + "F16", { "sketchPlane" : qUnion([Q0])});
            skLineSegment(sketch, "E79", {"start": v(0, 120) * mm, "end": v(0, 90) * mm, "construction": true});
            skPoint(sketch, "E79.startSnap0", {"position": v(0, 90) * mm});
            skCircle(sketch, "E80", {"center": v(0, 120) * mm, "radius": 6 * mm});
            skLineSegment(sketch, "E81", {"start": v(-33, 90) * mm, "end": v(-15, 108) * mm});
            skLineSegment(sketch, "E82", {"start": v(-15, 108) * mm, "end": v(-15, 120) * mm});
            skLineSegment(sketch, "E83", {"start": v(33, 90) * mm, "end": v(15, 108) * mm});
            skLineSegment(sketch, "E84", {"start": v(15, 108) * mm, "end": v(15, 120) * mm});
            skArc(sketch, "E85", {"start": v(15, 120) * mm, "mid": v(0, 135) * mm, "end": v(-15, 120) * mm});
            skLineSegment(sketch, "E86", {"start": v(-80, 0) * mm, "end": v(0, 0) * mm, "construction": true});
            skLineSegment(sketch, "E87", {"start": v(0, 0) * mm, "end": v(80, 0) * mm, "construction": true});
            skLineSegment(sketch, "E88", {"start": v(0, -120) * mm, "end": v(0, -90) * mm});
            skPoint(sketch, "E88.startSnap0", {"position": v(0, -90) * mm});
            skCircle(sketch, "E89", {"center": v(0, -120) * mm, "radius": 6 * mm});
            skLineSegment(sketch, "E90", {"start": v(33, -90) * mm, "end": v(15, -108) * mm});
            skLineSegment(sketch, "E91", {"start": v(15, -108) * mm, "end": v(15, -120) * mm});
            skLineSegment(sketch, "E92", {"start": v(-33, -90) * mm, "end": v(-15, -108) * mm});
            skLineSegment(sketch, "E93", {"start": v(-15, -108) * mm, "end": v(-15, -120) * mm});
            skArc(sketch, "E94", {"start": v(-15, -120) * mm, "mid": v(0, -135) * mm, "end": v(15, -120) * mm});
            skSolve(sketch);
        }
        {
            var Q0;
            Q0=makeQuery(id+"F16.imprint","IMPRINT",FACE,{"disambiguationData":[TD([[makeQuery(id+"F16.imprint","IMPRINT",EDGE,{"derivedFrom":makeQuery(id+"F1.opExtrude","CAP_EDGE",EDGE,{"disambiguationData":[OSD([sQuery(id+"F0.wireOp",EDGE,"E1.left")])],"isStart":true})}),-1.0]])]});
            var Q1;
            Q1=makeQuery(id+"F16.imprint","IMPRINT",FACE,{"disambiguationData":[TD([[makeQuery(id+"F16.imprint","IMPRINT",EDGE,{"derivedFrom":sQuery(id+"F16.wireOp",EDGE,"E80")}),-1.0]])]});
            var Q2;
            Q2=makeQuery(id+"F16.imprint","IMPRINT",FACE,{"disambiguationData":[TD([[makeQuery(id+"F16.imprint","IMPRINT",EDGE,{"derivedFrom":sQuery(id+"F16.wireOp",EDGE,"E89")}),-1.0]])]});
            var Q3;
            Q3=makeQuery(id+"F2.opExtrude","CAP_FACE",FACE,{"disambiguationData":[OSD([sQuery(id+"F0.wireOp",EDGE,"E12"),sQuery(id+"F0.wireOp",EDGE,"E13"),sQuery(id+"F0.wireOp",EDGE,"E14"),sQuery(id+"F0.wireOp",EDGE,"E15"),sQuery(id+"F0.wireOp",EDGE,"E17.filletArc"),sQuery(id+"F0.wireOp",EDGE,"E18.filletArc"),sQuery(id+"F0.wireOp",EDGE,"E19.filletArc"),sQuery(id+"F0.wireOp",EDGE,"E20.filletArc"),sQuery(id+"F0.wireOp",EDGE,"E25.0"),sQuery(id+"F0.wireOp",EDGE,"E25.1"),sQuery(id+"F0.wireOp",EDGE,"E25.2"),sQuery(id+"F0.wireOp",EDGE,"E25.3"),sQuery(id+"F0.wireOp",EDGE,"E25.4"),sQuery(id+"F0.wireOp",EDGE,"E25.5"),sQuery(id+"F0.wireOp",EDGE,"E25.6"),sQuery(id+"F0.wireOp",EDGE,"E25.7")])],"isStart":false});
            extrude(context, id + "F17", {"entities" : qUnion([Q0, Q1, Q2]), "endBound" : BoundingType.UP_TO_SURFACE, "endBoundEntityFace" : qUnion([Q3]), "depth" : 25 * mm});
        }
    });
